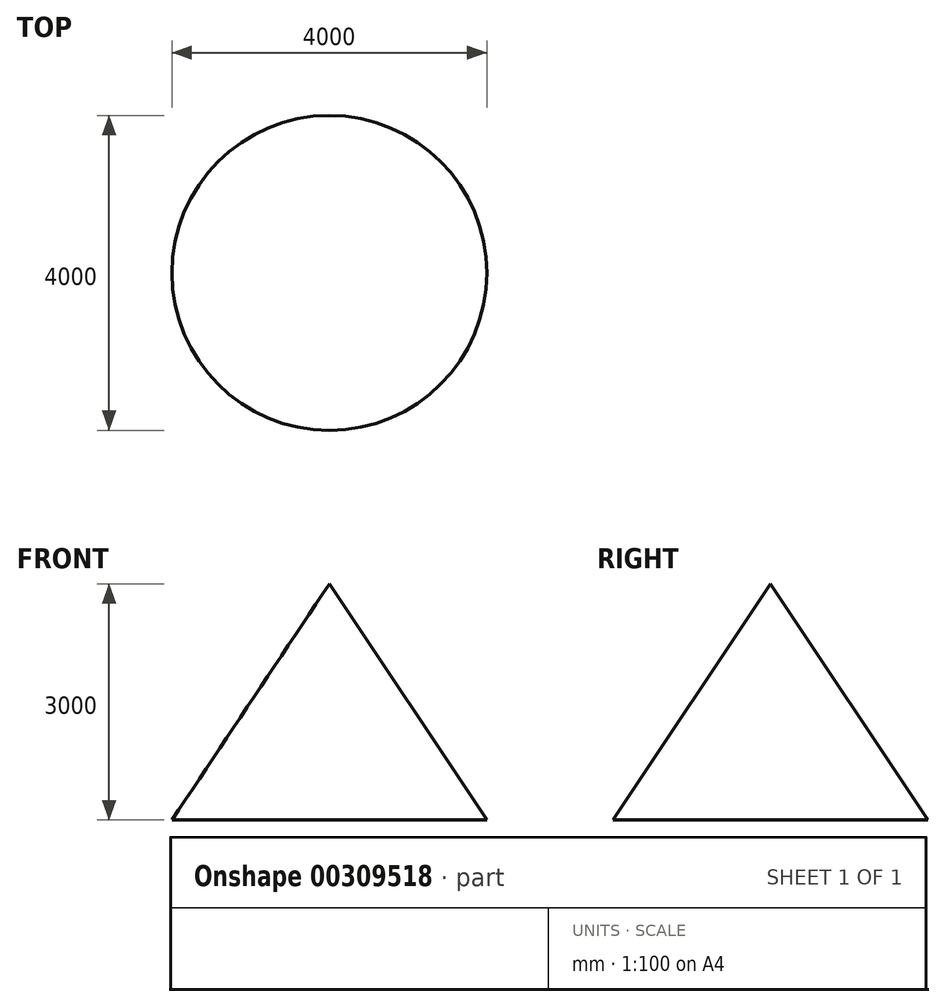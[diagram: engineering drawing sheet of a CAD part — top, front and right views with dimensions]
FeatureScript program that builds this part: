
annotation { "Feature Type Name" : "Feature", "Feature Type Description" : "" }
export const myFeature = defineFeature(function(context is Context, id is Id, definition is map)
    precondition{}
    {
        {
            var Q0;
            Q0=qCreatedBy(makeId("Front.planeOp"),FACE);
            var sketch = newSketch(context, id + "F0", { "sketchPlane" : qUnion([Q0])});
            skLineSegment(sketch, "E0", {"start": v(0, 0) * mm, "end": v(-2000, 0) * mm});
            skLineSegment(sketch, "E1", {"start": v(-2000, 0) * mm, "end": v(0, 3000) * mm});
            skLineSegment(sketch, "E2", {"start": v(0, 3000) * mm, "end": v(0, 0) * mm});
            skLineSegment(sketch, "E3", {"start": v(0, 0) * mm, "end": v(0, 60.37) * mm, "construction": true});
            skSolve(sketch);
        }
        {
            var Q0;
            Q0 = qSketchRegion(id + "F0", true);
            var Q1;
            Q1=sQuery(id+"F0.wireOp",EDGE,"E2");
            revolve(context, id + "F1", {"entities" : qUnion([Q0]), "axis" : qUnion([Q1]), "revolveType" : RevolveType.FULL});
        }
    });
